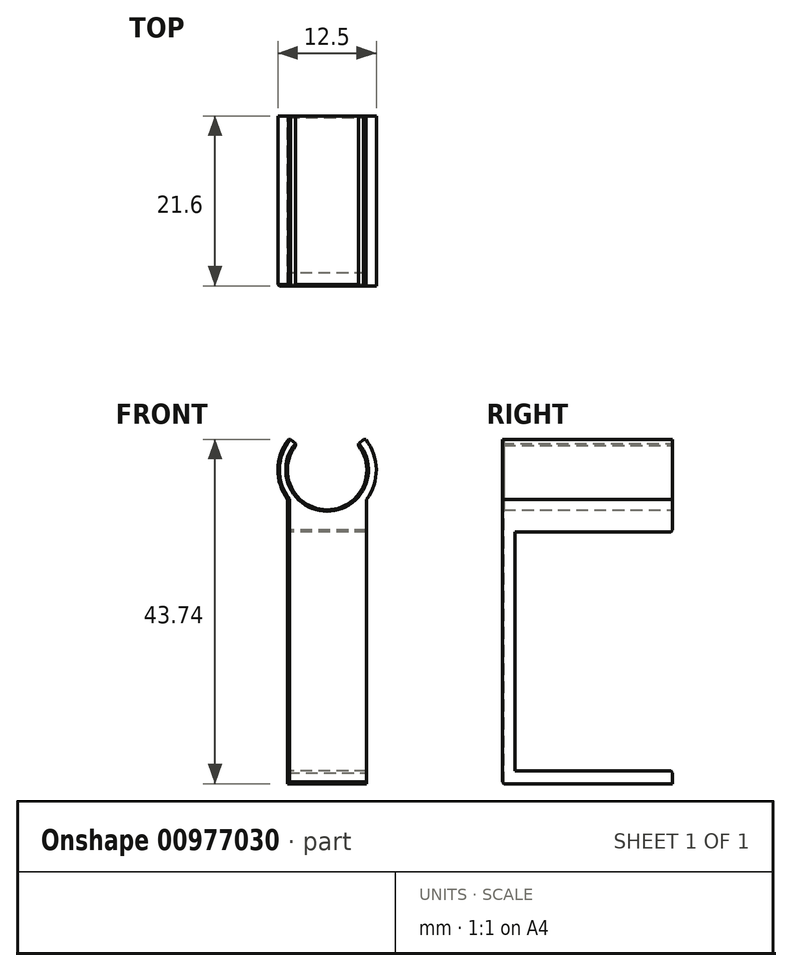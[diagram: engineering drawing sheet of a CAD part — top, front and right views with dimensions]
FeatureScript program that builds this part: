
annotation { "Feature Type Name" : "Feature", "Feature Type Description" : "" }
export const myFeature = defineFeature(function(context is Context, id is Id, definition is map)
    precondition{}
    {
        {
            var Q0;
            Q0=qCreatedBy(makeId("Right.planeOp"),FACE);
            var sketch = newSketch(context, id + "F0", { "sketchPlane" : qUnion([Q0])});
            skLineSegment(sketch, "E0", {"start": v(0, 15.2) * mm, "end": v(0, -15.2) * mm});
            skLineSegment(sketch, "E1", {"start": v(0, -15.2) * mm, "end": v(20, -15.2) * mm});
            skLineSegment(sketch, "E2", {"start": v(20, -15.2) * mm, "end": v(20, -16.8) * mm});
            skLineSegment(sketch, "E3", {"start": v(20, -16.8) * mm, "end": v(-1.6, -16.8) * mm});
            skLineSegment(sketch, "E4", {"start": v(-1.6, -16.8) * mm, "end": v(-1.6, 16.8) * mm});
            skLineSegment(sketch, "E5", {"start": v(-1.6, 16.8) * mm, "end": v(20, 16.8) * mm});
            skLineSegment(sketch, "E6", {"start": v(20, 16.8) * mm, "end": v(20, 15.2) * mm});
            skLineSegment(sketch, "E7", {"start": v(20, 15.2) * mm, "end": v(0, 15.2) * mm});
            skSolve(sketch);
        }
        {
            var Q0;
            Q0 = qSketchRegion(id + "F0", true);
            extrude(context, id + "F1", {"entities" : qUnion([Q0]), "endBound" : BoundingType.SYMMETRIC, "depth" : 10 * mm, "offsetDistance" : 25 * mm});
        }
        {
            var Q0;
            Q0=qCreatedBy(makeId("Front.planeOp"),FACE);
            var sketch = newSketch(context, id + "F2", { "sketchPlane" : qUnion([Q0])});
            skLineSegment(sketch, "E8.0", {"start": v(5, 16.8) * mm, "end": v(-5, 16.8) * mm});
            skArc(sketch, "E9", {"start": v(-4.79, 27.07) * mm, "mid": v(-6.25, 23.22) * mm, "end": v(-5, 19.3) * mm});
            skArc(sketch, "E10", {"start": v(-3.87, 26.3) * mm, "mid": v(0, 18) * mm, "end": v(3.87, 26.3) * mm});
            skLineSegment(sketch, "E11", {"start": v(-3.87, 26.3) * mm, "end": v(-4.79, 27.07) * mm});
            skLineSegment(sketch, "E12.MirrorCS", {"start": v(3.87, 26.3) * mm, "end": v(4.79, 27.07) * mm});
            skLineSegment(sketch, "E13", {"start": v(-5, 16.8) * mm, "end": v(-5, 19.3) * mm});
            skLineSegment(sketch, "E14", {"start": v(5, 16.8) * mm, "end": v(5, 19.3) * mm});
            skArc(sketch, "E15.trimOffspring", {"start": v(5, 19.3) * mm, "mid": v(6.25, 23.22) * mm, "end": v(4.79, 27.07) * mm});
            skSolve(sketch);
        }
        {
            var Q0;
            Q0=makeQuery(id+"F2.imprint","IMPRINT",FACE,{"disambiguationData":[TD([[makeQuery(id+"F2.imprint","IMPRINT",EDGE,{"derivedFrom":sQuery(id+"F2.wireOp",EDGE,"E8.0")}),-1.0]])]});
            extrude(context, id + "F3", {"entities" : qUnion([Q0]), "operationType" : NewBodyOperationType.ADD, "depth" : 1.6 * mm, "offsetDistance" : 25 * mm, "hasSecondDirection" : true, "secondDirectionOppositeDirection" : true, "secondDirectionDepth" : 20 * mm});
        }
        {
            var Q0;
            Q0=makeQuery(id+"F1.opExtrude","SWEPT_EDGE",EDGE,{"disambiguationData":[OSD([sQuery(id+"F0.wireOp",EDGE,"E6"),sQuery(id+"F0.wireOp",EDGE,"E7")])]});
            var Q1;
            Q1=makeQuery(id+"F1.opExtrude","SWEPT_EDGE",EDGE,{"disambiguationData":[OSD([sQuery(id+"F0.wireOp",EDGE,"E1"),sQuery(id+"F0.wireOp",EDGE,"E2")])]});
            var Q2;
            Q2=makeQuery(id+"F1.opExtrude","SWEPT_EDGE",EDGE,{"disambiguationData":[OSD([sQuery(id+"F0.wireOp",EDGE,"E3"),sQuery(id+"F0.wireOp",EDGE,"E4")])]});
            var Q3;
            Q3=makeQuery(id+"F3.opExtrude","CAP_EDGE",EDGE,{"disambiguationData":[OSD([sQuery(id+"F2.wireOp",EDGE,"E10")])],"isStart":false});
            var Q4;
            Q4=makeQuery(id+"F3.opExtrude","CAP_EDGE",EDGE,{"disambiguationData":[OSD([sQuery(id+"F2.wireOp",EDGE,"E9")])],"isStart":false});
            var Q5;
            Q5=makeQuery(id+"F3.boolean.opBoolean","MERGE",EDGE,{"derivedFrom":[makeQuery(id+"F1.opExtrude","CAP_EDGE",EDGE,{"disambiguationData":[OSD([sQuery(id+"F0.wireOp",EDGE,"E4")])],"isStart":true}),makeQuery(id+"F3.opExtrude","CAP_EDGE",EDGE,{"disambiguationData":[OSD([sQuery(id+"F2.wireOp",EDGE,"E13")])],"isStart":false})]});
            var Q6;
            Q6=makeQuery(id+"F3.opExtrude","SWEPT_EDGE",EDGE,{"disambiguationData":[OSD([sQuery(id+"F2.wireOp",EDGE,"E10"),sQuery(id+"F2.wireOp",EDGE,"E12.MirrorCS")])]});
            var Q7;
            Q7=makeQuery(id+"F3.opExtrude","SWEPT_EDGE",EDGE,{"disambiguationData":[OSD([sQuery(id+"F2.wireOp",EDGE,"E10"),sQuery(id+"F2.wireOp",EDGE,"E11")])]});
            var Q8;
            Q8=makeQuery(id+"F3.opExtrude","SWEPT_EDGE",EDGE,{"disambiguationData":[OSD([sQuery(id+"F2.wireOp",EDGE,"E9"),sQuery(id+"F2.wireOp",EDGE,"E11")])]});
            var Q9;
            Q9=makeQuery(id+"F3.opExtrude","SWEPT_EDGE",EDGE,{"disambiguationData":[OSD([sQuery(id+"F2.wireOp",EDGE,"E12.MirrorCS"),sQuery(id+"F2.wireOp",EDGE,"E15.trimOffspring")])]});
            chamfer(context, id + "F4", {"entities" : qUnion([Q0, Q1, Q2, Q3, Q4, Q5, Q6, Q7, Q8, Q9]), "width" : 0.2 * mm, "tangentPropagation" : true});
        }
    });
